# Revit family: Reece_Tap_Grohe_Essence New_Basin Mixer_Extended_Gooseneck
name_source: partatom
category: Plumbing Fixtures
revit_build: Autodesk Revit 2018 (Build: 20180329_1100(x64)
units: mm (PartAtom-declared; Revit-internal decimal feet)

## family parameters
Cut with Voids When Loaded = No
Host = Face
Part Type = Normal
Room Calculation Point = Yes
Round Connector Dimension = Use Diameter
Shared = Yes

## types (1)
- Chrome
    CWFU = 0
    Default Elevation = 1000 mm  [stored 3.28084 ft]
    Description = Grohe Essence New Extended Gooseneck Basin Mixer (6 Star) Chrome
    Disclaimer = THIS FILE IS THE PROPERTY OF THE REECE GROUP. IT MAY NOT BE REPRODUCED, REVERSE-ENGINEERED OR MODIFIED. ANY REPUBLICATION, TRANSMISSION OR DISTRIBUTION FOR THE PURPOSE OF COMMERCIALLY EXPLOITING THE FILES IS PROHIBITED.
    HWFU = 0
    Keynote = Product #9508959, Reece_Tap_Grohe_Essence New_Basin Mixer_Extended_Gooseneck - Chrome
    Manufacturer = Grohe
    Model = Essence New
    Reece_Detail_Additional = Extended
    Reece_Detail_Disclaimer = THIS FILE IS THE PROPERTY OF THE REECE GROUP. IT MAY NOT BE REPRODUCED, REVERSE-ENGINEERED OR MODIFIED. ANY REPUBLICATION, TRANSMISSION OR DISTRIBUTION FOR THE PURPOSE OF COMMERCIALLY EXPLOITING THE FILES IS PROHIBITED.
    Reece_Detail_Installation = Basin Mixer
    Reece_Detail_Shape = Gooseneck
    Reece_Material_Main = Reece_Brass_Chrome
    Reece_Material_Tap_Cold = Render_Cold_Water_Cap
    Reece_Material_Tap_Hot = Render_Hot_Water_Cap
    Reece_Overall_Height = 364 mm  [stored 1.19423 ft]
    Reece_Product_Brand = Grohe
    Reece_Product_Description = GROHE Essence New Extended Gooseneck Basin Mixer Chrome (6 Star)
    Reece_Product_Mount = Hob Mounted
    Reece_Product_Number = 9508959
    Reece_Product_Sub Brand = Essence New
    Reece_Product_Type = Tap
    Reece_Product_Web Page = https://www.reece.com.au
    Reece_Stand_Baseplate_Radius = 24 mm  [stored 0.0787402 ft]
    Reece_Stand_Radius = 22 mm
    Reece_Tap_Clearance = 322 mm  [stored 1.05643 ft]
    Reece_Tap_Inlet = 12 mm  [stored 0.0393701 ft]
    Reece_Tap_Reach = 179 mm  [stored 0.58727 ft]
    Type Comments = Tap
    URL = https://www.reece.com.au
    WFU = 0

note: [stored X ft] marks values corroborated as IEEE doubles in the binary element streams (Revit-internal decimal feet)

## geometry (parser evidence)
native form markers: Sweep x3
no freeform markers — native parametric forms only
